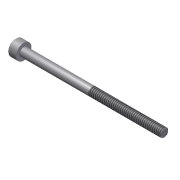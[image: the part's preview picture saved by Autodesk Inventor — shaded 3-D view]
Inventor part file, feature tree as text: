
AUTODESK INVENTOR PART (.ipt)
format: ipt  version: 2011 (Build 150239000, 239)  size: 89,600 bytes
history: native  units: in
note: dims shown in document units (in); Inventor stores cm internally (conversion verified against a paired STEP export)
features: other x1, imported_body x1, thread x1
ambient origin geometry x8: Origin, YZ Plane, XZ Plane, XY Plane, X Axis, Y Axis, Z Axis, Center Point
feature tree (3):
  other  "Hex"
  imported_body  "Base1"
  thread  "Thread1"  [1 undecoded]
note: 1 required parameter value undecoded (feature->parameter linkage not recoverable at this tier; creation-order binding heuristic only, values carry confidence <= 0.55)
